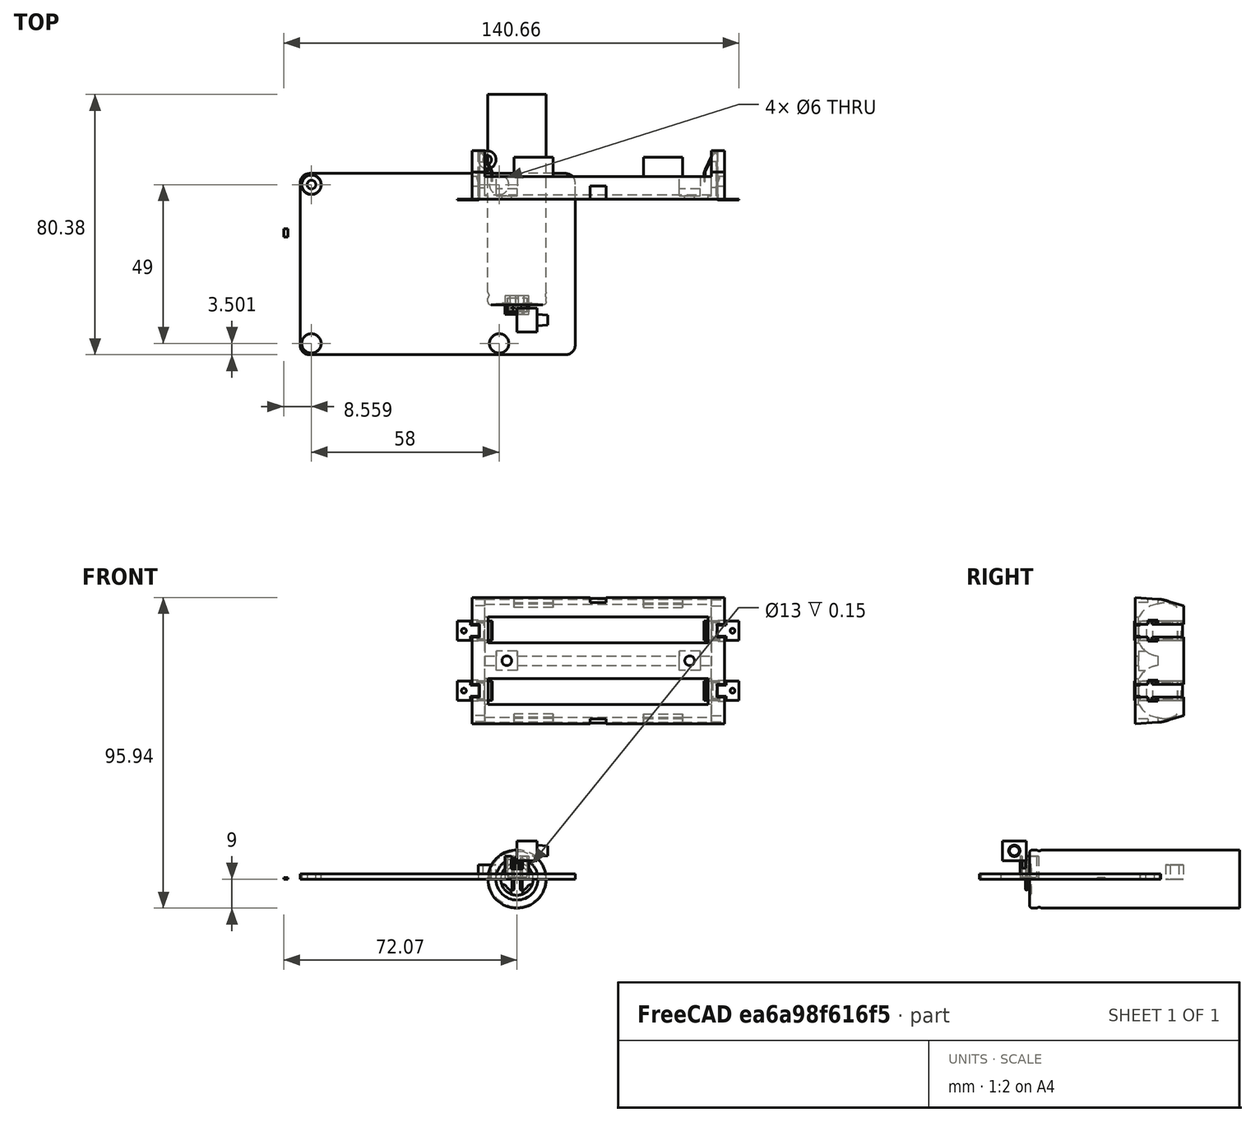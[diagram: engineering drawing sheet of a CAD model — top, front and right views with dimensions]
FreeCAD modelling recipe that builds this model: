
FCSTD DOCUMENT  (FreeCAD 1.0R39109 (Git))
Label: UPS
License: All rights reserved
LicenseURL: https://en.wikipedia.org/wiki/All_rights_reserved
objects: App::FeaturePython×23, App::Link×22, Part::Feature×12, Sketcher::SketchObject×6, PartDesign::Pad×6, PartDesign::Body×5, App::Part×4, PartDesign::Chamfer×1, Assembly::JointGroup×1, Assembly::AssemblyObject×1
note: 50 computed .brp shape members not serialized (recipe doc carries the construction recipe); baked Part::Feature solids carry a one-line shape summary decoded from their .brp

FEATURE [Sketcher::SketchObject] Sketch
  ArcFitTolerance = 1e-06
  FullyConstrained = false
  MakeInternals = false
  sketch-geometry (20):
    g0: LineSegment StartX=-64.0111 StartY=-15.3795 StartZ=0 EndX=14.9889 EndY=-15.3795 EndZ=0
    g1: LineSegment StartX=17.9889 StartY=-12.3795 StartZ=0 EndX=17.9889 EndY=37.6205 EndZ=0
    g2: LineSegment StartX=14.9889 StartY=40.6205 StartZ=0 EndX=-64.0111 EndY=40.6205 EndZ=0
    g3: LineSegment StartX=-67.0111 StartY=37.6205 StartZ=0 EndX=-67.0111 EndY=-12.3795 EndZ=0
    g4: ArcOfCircle CenterX=14.9889 CenterY=37.6205 CenterZ=0 NormalX=0 NormalY=0 NormalZ=1 AngleXU=0 Radius=3 StartAngle=5e-16 EndAngle=1.5708
    g5: GeomPoint [constr] X=17.9889 Y=40.6205 Z=0
    g6: ArcOfCircle CenterX=-64.0111 CenterY=37.6205 CenterZ=0 NormalX=0 NormalY=0 NormalZ=1 AngleXU=0 Radius=3 StartAngle=1.5708 EndAngle=3.14159
    g7: GeomPoint [constr] X=-67.0111 Y=40.6205 Z=0
    g8: ArcOfCircle CenterX=-64.0111 CenterY=-12.3795 CenterZ=0 NormalX=0 NormalY=0 NormalZ=1 AngleXU=0 Radius=3 StartAngle=3.14159 EndAngle=4.71239
    g9: GeomPoint [constr] X=-67.0111 Y=-15.3795 Z=0
    g10: ArcOfCircle CenterX=14.9889 CenterY=-12.3795 CenterZ=0 NormalX=0 NormalY=0 NormalZ=1 AngleXU=0 Radius=3 StartAngle=4.71239 EndAngle=6.28319
    g11: GeomPoint [constr] X=17.9889 Y=-15.3795 Z=0
    g12: Circle CenterX=-63.5111 CenterY=37.1205 CenterZ=0 NormalX=0 NormalY=0 NormalZ=1 AngleXU=0 Radius=1.35
    g13: Circle CenterX=-63.5111 CenterY=37.1205 CenterZ=0 NormalX=0 NormalY=0 NormalZ=1 AngleXU=0 Radius=3
    g14: Circle CenterX=-63.5111 CenterY=-11.8795 CenterZ=0 NormalX=0 NormalY=0 NormalZ=1 AngleXU=0 Radius=1.35
    g15: Circle CenterX=-63.5111 CenterY=-11.8795 CenterZ=0 NormalX=0 NormalY=0 NormalZ=1 AngleXU=0 Radius=3
    g16: Circle CenterX=-5.51111 CenterY=37.1205 CenterZ=0 NormalX=0 NormalY=0 NormalZ=1 AngleXU=0 Radius=1.35
    g17: Circle CenterX=-5.51111 CenterY=37.1205 CenterZ=0 NormalX=0 NormalY=0 NormalZ=1 AngleXU=0 Radius=3
    g18: Circle CenterX=-5.51111 CenterY=-11.8795 CenterZ=0 NormalX=0 NormalY=0 NormalZ=1 AngleXU=0 Radius=1.35
    g19: Circle CenterX=-5.51111 CenterY=-11.8795 CenterZ=0 NormalX=0 NormalY=0 NormalZ=1 AngleXU=0 Radius=3
  constraints (46):
    c: Horizontal(g0)
    c: Horizontal(g2)
    c: Vertical(g1)
    c: Vertical(g3)
    c: DistanceX(g7,g5) = 85
    c: DistanceY(g9,g7) = 56
    c: PointOnObject(g5,g1)
    c: PointOnObject(g5,g2)
    c: Tangent(g1,g4) = -1.5708
    c: Tangent(g2,g4) = -1.5708
    c: PointOnObject(g7,g2)
    c: PointOnObject(g7,g3)
    c: Tangent(g2,g6) = -1.5708
    c: Tangent(g3,g6) = -1.5708
    c: PointOnObject(g9,g0)
    c: PointOnObject(g9,g3)
    c: Tangent(g0,g8) = -1.5708
    c: Tangent(g3,g8) = -1.5708
    c: PointOnObject(g11,g0)
    c: PointOnObject(g11,g1)
    c: Tangent(g0,g10) = -1.5708
    c: Tangent(g1,g10) = -1.5708
    c: Radius(g6) = 3
    c: Radius(g8) = 3
    c: Radius(g4) = 3
    c: Radius(g10) = 3
    c: Diameter(g12) = 2.7
    c: Coincident(g13,g12)
    c: Diameter(g13) = 6
    c: Diameter(g14) = 2.7
    c: Coincident(g15,g14)
    c: Diameter(g15) = 6
    c: Vertical(g14,g12)
    c: Distance(g13,g15) = 43
    c: Distance(g13,g3) = 0.5
    c: Distance(g13,g2) = 0.5
    c: Diameter(g16) = 2.7
    c: Coincident(g17,g16)
    c: Diameter(g17) = 6
    c: Diameter(g18) = 2.7
    c: Coincident(g19,g18)
    c: Diameter(g19) = 6
    c: Vertical(g18,g16)
    c: Distance(g17,g19) = 43
    c: Distance(g15,g19) = 52
    c: Horizontal(g18,g14)
FEATURE [PartDesign::Pad] Pad
  Direction = (0,0,1)
  Length = 1.6
  Length2 = 10
  Profile = -> Sketch
  ReferenceAxis = -> Sketch [N_Axis]
  Refine = true
  Suppressed = false
  Type = 0
FEATURE [PartDesign::Body] Body  label="Board"
  AllowCompound = false
  Group = -> [Sketch,Pad]
  Origin = -> Origin
  Tip = -> Pad
FEATURE [Sketcher::SketchObject] Sketch001
  ArcFitTolerance = 1e-06
  AttachmentSupport = -> [XY_Plane003]
  FullyConstrained = false
  MakeInternals = false
  MapMode = 5
  sketch-geometry (2):
    g0: Circle CenterX=-63.4811 CenterY=37.1626 CenterZ=0 NormalX=0 NormalY=0 NormalZ=1 AngleXU=0 Radius=3
    g1: Circle CenterX=-63.4811 CenterY=37.1626 CenterZ=0 NormalX=0 NormalY=0 NormalZ=1 AngleXU=0 Radius=1.35
  constraints (3):
    c: Diameter(g0) = 6
    c: Coincident(g1,g0)
    c: Diameter(g1) = 2.7
FEATURE [PartDesign::Pad] Pad001
  Direction = (0,0,1)
  Length = 1.6
  Length2 = 10
  Profile = -> Sketch001
  ReferenceAxis = -> Sketch001 [N_Axis]
  Refine = true
  Suppressed = false
  Type = 0
FEATURE [PartDesign::Body] Body001  label="Screw Insert"
  AllowCompound = false
  Group = -> [Sketch001,Pad001]
  Origin = -> Origin003
  Tip = -> Pad001
FEATURE [Part::Feature] Part__Feature  label="Battery Holder"
  Placement = pos=(25.0935,32.6929,67.437) rot=(0,0,1;0rad)
  shape: bbox 78 x 15 x 39 mm, 194 faces (baked)
FEATURE [Part::Feature] Part__Feature001  label="Battery-Holder_Metal-Lead"
  Placement = pos=(66.5935,32.3929,76.687) rot=(0,0,1;0rad)
  shape: bbox 10.8 x 15.51 x 6 mm, 51 faces (baked)
FEATURE [Part::Feature] Part__Feature002  label="Battery-Holder_Metal-Lead001"
  Placement = pos=(66.5935,32.3929,58.187) rot=(0,0,1;0rad)
  shape: bbox 10.8 x 15.51 x 6 mm, 51 faces (baked)
FEATURE [Part::Feature] Part__Feature003  label="Battery-Holder_Metal-Lead002"
  Placement = pos=(-16.4065,32.3929,58.187) rot=(0,1,0;3.14159rad)
  shape: bbox 10.8 x 15.51 x 6 mm, 51 faces (baked)
FEATURE [Part::Feature] Part__Feature004  label="Battery-Holder_Metal-Lead003"
  Placement = pos=(-16.4065,32.3929,76.687) rot=(0,1,0;3.14159rad)
  shape: bbox 10.8 x 15.51 x 6 mm, 51 faces (baked)
FEATURE [App::Part] Assem1  label="18650 Battery Holder"
  Group = -> [Part__Feature,Part__Feature001,Part__Feature002,Part__Feature003,Part__Feature004]
  Origin = -> Origin004
FEATURE [Part::Feature] Part__Feature005  label="18650 v1"
  shape: bbox 19.48 x 65 x 19.48 mm, 40 faces (baked)
FEATURE [App::FeaturePython] Temporary_joint  # Assembly joint (typed FeaturePython)
  Activated = true
  AngleMax = 0
  AngleMin = 0
  Detach1 = false
  Detach2 = false
  Distance = 0
  Distance2 = 0
  EnableAngleMax = false
  EnableAngleMin = false
  EnableLengthMax = false
  EnableLengthMin = false
  JointType = 0 (Fixed)
  LengthMax = 0
  LengthMin = 0
FEATURE [App::Link] Board  label="Board001"
  LinkedObject = -> Body
FEATURE [App::FeaturePython] GroundedJoint  # Assembly grounded joint (typed FeaturePython)
  ObjectToGround = -> Board
FEATURE [App::Link] _8650_Battery_Holder  label="18650 Battery Holder001"
  LinkPlacement = pos=(-46.1046,82.0575,-31.0929) rot=(1,0,0;1.5708rad)
  LinkedObject = -> Assem1
  Placement = pos=(-46.1046,82.0575,-31.0929) rot=(1,0,0;1.5708rad)
FEATURE [App::Link] Screw_Insert  label="Screw Insert001"
  LinkPlacement = pos=(-0.030029,-0.0421514,0) rot=(0,0,1;0rad)
  LinkedObject = -> Body001
  Placement = pos=(-0.030029,-0.0421514,0) rot=(0,0,1;0rad)
FEATURE [App::Link] Screw_Insert001  label="Screw Insert002"
  LinkPlacement = pos=(-0.030029,-49.0422,1e-16) rot=(0,0,1;0rad)
  LinkedObject = -> Body001
  Placement = pos=(-0.030029,-49.0422,1e-16) rot=(0,0,1;0rad)
FEATURE [App::Link] Screw_Insert002  label="Screw Insert003"
  LinkPlacement = pos=(57.97,-49.0422,-1e-16) rot=(0,0,1;0rad)
  LinkedObject = -> Body001
  Placement = pos=(57.97,-49.0422,-1e-16) rot=(0,0,1;0rad)
FEATURE [App::Link] Screw_Insert003  label="Screw Insert004"
  LinkPlacement = pos=(57.97,-0.0421514,0) rot=(0,0,1;0rad)
  LinkedObject = -> Body001
  Placement = pos=(57.97,-0.0421514,0) rot=(0,0,1;0rad)
FEATURE [App::FeaturePython] Joint  label="Fixed"  # Assembly joint (typed FeaturePython)
  Activated = true
  AngleMax = 0
  AngleMin = 0
  Detach1 = false
  Detach2 = false
  Distance = 0
  Distance2 = 0
  EnableAngleMax = false
  EnableAngleMin = false
  EnableLengthMax = false
  EnableLengthMin = false
  JointType = 0 (Fixed)
  LengthMax = 0
  LengthMin = 0
  Placement1 = pos=(-63.4811,37.1626,1.6) rot=(0,0,1;0rad)
  Placement2 = pos=(-63.5111,37.1205,1.6) rot=(0,0,1;0rad)
  Reference1 = -> Assembly [Screw_Insert.Edge3,Screw_Insert.Edge3]
  Reference2 = -> Assembly [Board.Edge36,Board.Edge36]
FEATURE [App::FeaturePython] Joint001  label="Fixed001"  # Assembly joint (typed FeaturePython)
  Activated = true
  AngleMax = 0
  AngleMin = 0
  Detach1 = false
  Detach2 = false
  Distance = 0
  Distance2 = 0
  EnableAngleMax = false
  EnableAngleMin = false
  EnableLengthMax = false
  EnableLengthMin = false
  JointType = 0 (Fixed)
  LengthMax = 0
  LengthMin = 0
  Placement1 = pos=(-63.4811,37.1626,1.6) rot=(0,0,1;0rad)
  Placement2 = pos=(-63.5111,-11.8795,1.6) rot=(0,0,1;0rad)
  Reference1 = -> Assembly [Screw_Insert001.Edge3,Screw_Insert001.Edge3]
  Reference2 = -> Assembly [Board.Edge33,Board.Edge33]
FEATURE [App::FeaturePython] Joint002  label="Fixed002"  # Assembly joint (typed FeaturePython)
  Activated = true
  AngleMax = 0
  AngleMin = 0
  Detach1 = false
  Detach2 = false
  Distance = 0
  Distance2 = 0
  EnableAngleMax = false
  EnableAngleMin = false
  EnableLengthMax = false
  EnableLengthMin = false
  JointType = 0 (Fixed)
  LengthMax = 0
  LengthMin = 0
  Placement1 = pos=(-63.4811,37.1626,1.6) rot=(0,0,1;0rad)
  Placement2 = pos=(-5.51111,-11.8795,1.6) rot=(0,0,1;0rad)
  Reference1 = -> Assembly [Screw_Insert002.Edge3,Screw_Insert002.Edge3]
  Reference2 = -> Assembly [Board.Edge27,Board.Edge27]
FEATURE [App::FeaturePython] Joint003  label="Fixed003"  # Assembly joint (typed FeaturePython)
  Activated = true
  AngleMax = 0
  AngleMin = 0
  Detach1 = false
  Detach2 = false
  Distance = 0
  Distance2 = 0
  EnableAngleMax = false
  EnableAngleMin = false
  EnableLengthMax = false
  EnableLengthMin = false
  JointType = 0 (Fixed)
  LengthMax = 0
  LengthMin = 0
  Placement1 = pos=(-63.4811,37.1626,1.6) rot=(0,0,1;0rad)
  Placement2 = pos=(-5.51111,37.1205,1.6) rot=(0,0,1;0rad)
  Reference1 = -> Assembly [Screw_Insert003.Edge3,Screw_Insert003.Edge3]
  Reference2 = -> Assembly [Board.Edge30,Board.Edge30]
FEATURE [Part::Feature] Part__Feature006  label="XH 2,54_2p"
  shape: bbox 7.4 x 5.75 x 7 mm, 52 faces (baked)
FEATURE [Part::Feature] Part__Feature007  label="XH 2,54_2p001"
  shape: bbox 0.64 x 0.64 x 9.7 mm, 14 faces (baked)
FEATURE [Part::Feature] Part__Feature008  label="XH 2,54_2p002"
  shape: bbox 0.64 x 0.64 x 9.7 mm, 14 faces (baked)
FEATURE [App::Part] XH_2_54_2p  label="XH 2,54_2p003"
  Group = -> [Part__Feature006,Part__Feature007,Part__Feature008]
  Origin = -> Origin006
FEATURE [Part::Feature] Part__Feature009  label="XH 2,54_2p004"
  shape: bbox 7.4 x 5.75 x 7 mm, 52 faces (baked)
FEATURE [Part::Feature] Part__Feature010  label="XH 2,54_2p005"
  shape: bbox 0.64 x 0.64 x 9.7 mm, 14 faces (baked)
FEATURE [Part::Feature] Part__Feature011  label="XH 2,54_2p006"
  shape: bbox 0.64 x 0.64 x 9.7 mm, 14 faces (baked)
FEATURE [App::Part] XH_2_54_2p001  label="XH 2,54_2p007"
  Group = -> [Part__Feature009,Part__Feature010,Part__Feature011]
  Origin = -> Origin007
FEATURE [App::Link] XH_2_54_2p007  label="XH 2,54_2p008"
  LinkPlacement = pos=(-33.6111,-12.3795,1.6) rot=(0,0,1;0rad)
  LinkedObject = -> XH_2_54_2p001
  Placement = pos=(-33.6111,-12.3795,1.6) rot=(0,0,1;0rad)
FEATURE [App::Link] XH_2_54_2p008  label="XH 2,54_2p009"
  LinkPlacement = pos=(5.78889,-12.3795,1.6) rot=(0,0,1;0rad)
  LinkedObject = -> XH_2_54_2p001
  Placement = pos=(5.78889,-12.3795,1.6) rot=(0,0,1;0rad)
FEATURE [App::FeaturePython] Joint004  label="Fixed004"  # Assembly joint (typed FeaturePython)
  Activated = true
  AngleMax = 0
  AngleMin = 0
  Detach1 = false
  Detach2 = false
  Distance = 0
  Distance2 = 0
  EnableAngleMax = false
  EnableAngleMin = false
  EnableLengthMax = false
  EnableLengthMin = false
  JointType = 0 (Fixed)
  LengthMax = 0
  LengthMin = 0
  Offset1 = pos=(0,8.5,0) rot=(0,0,1;0rad)
  Placement1 = pos=(12.2,0,0) rot=(0.57735,0.57735,0.57735;4.18879rad)
  Placement2 = pos=(17.9889,-12.3795,1.6) rot=(0.57735,0.57735,0.57735;4.18879rad)
  Reference1 = -> Assembly [XH_2_54_2p008.Part__Feature009.Edge98,XH_2_54_2p008.Part__Feature009.Edge98]
  Reference2 = -> Assembly [Board.Edge10,Board.Vertex6]
FEATURE [App::FeaturePython] Joint005  label="Fixed005"  # Assembly joint (typed FeaturePython)
  Activated = true
  AngleMax = 0
  AngleMin = 0
  Detach1 = false
  Detach2 = false
  Distance = 0
  Distance2 = 0
  EnableAngleMax = false
  EnableAngleMin = false
  EnableLengthMax = false
  EnableLengthMin = false
  JointType = 0 (Fixed)
  LengthMax = 0
  LengthMin = 0
  Offset1 = pos=(0,32,0) rot=(0,0,1;0rad)
  Offset2 = pos=(0,0,0) rot=(0,0,1;3.14159rad)
  Placement1 = pos=(35.7,0,0) rot=(0.57735,0.57735,0.57735;4.18879rad)
  Placement2 = pos=(-3.7,0,0) rot=(-0.57735,0.57735,-0.57735;4.18879rad)
  Reference1 = -> Assembly [XH_2_54_2p007.Part__Feature009.Edge98,XH_2_54_2p007.Part__Feature009.Edge98]
  Reference2 = -> Assembly [XH_2_54_2p008.Part__Feature009.Edge75,XH_2_54_2p008.Part__Feature009.Edge75]
FEATURE [App::FeaturePython] Joint006  label="Fixed006"  # Assembly joint (typed FeaturePython)
  Activated = true
  AngleMax = 0
  AngleMin = 0
  Detach1 = false
  Detach2 = false
  Distance = 0
  Distance2 = 0
  EnableAngleMax = false
  EnableAngleMin = false
  EnableLengthMax = false
  EnableLengthMin = false
  JointType = 0 (Fixed)
  LengthMax = 0
  LengthMin = 0
  Offset2 = pos=(0,0,2) rot=(0,0,-1;1.5708rad)
  Placement1 = pos=(39,7.1e-15,0) rot=(0,1,0;3.14159rad)
  Placement2 = pos=(17.9889,14.6205,1.6) rot=(0,0.707107,0.707107;3.14159rad)
  Reference1 = -> Assembly [_8650_Battery_Holder.Part__Feature.Edge41,_8650_Battery_Holder.Part__Feature.Edge41]
  Reference2 = -> Assembly [Board.Edge10,Board.Edge10]
FEATURE [App::Link] _8650_v1  label="18650 v002"
  LinkPlacement = pos=(11.2889,5.37045,11.2138) rot=(0,0,1;1.5708rad)
  LinkedObject = -> Part__Feature005
  Placement = pos=(11.2889,5.37045,11.2138) rot=(0,0,1;1.5708rad)
FEATURE [App::Link] _8650_v002  label="18650 v003"
  LinkPlacement = pos=(11.2889,23.8705,11.2138) rot=(0,0,1;1.5708rad)
  LinkedObject = -> Part__Feature005
  Placement = pos=(11.2889,23.8705,11.2138) rot=(0,0,1;1.5708rad)
FEATURE [App::FeaturePython] Joint007  label="Fixed007"  # Assembly joint (typed FeaturePython)
  Activated = true
  AngleMax = 0
  AngleMin = 0
  Detach1 = false
  Detach2 = false
  Distance = 0
  Distance2 = 0
  EnableAngleMax = false
  EnableAngleMin = false
  EnableLengthMax = false
  EnableLengthMin = false
  JointType = 0 (Fixed)
  LengthMax = 0
  LengthMin = 0
  Offset1 = pos=(-3,0,0) rot=(0,0,1;0rad)
  Placement1 = pos=(-5e-16,65,-3) rot=(-0.57735,-0.57735,-0.57735;2.0944rad)
  Placement2 = pos=(-8.8,6.91375,0) rot=(-0.57735,-0.57735,-0.57735;4.18879rad)
  Reference1 = -> Assembly [_8650_v1.Face35,_8650_v1.Edge1]
  Reference2 = -> Assembly [_8650_Battery_Holder.Part__Feature004.Face22,_8650_Battery_Holder.Part__Feature004.Face22]
FEATURE [App::FeaturePython] Joint008  label="Fixed008"  # Assembly joint (typed FeaturePython)
  Activated = true
  AngleMax = 0
  AngleMin = 0
  Detach1 = false
  Detach2 = false
  Distance = 0
  Distance2 = 0
  EnableAngleMax = false
  EnableAngleMin = false
  EnableLengthMax = false
  EnableLengthMin = false
  JointType = 0 (Fixed)
  LengthMax = 0
  LengthMin = 0
  Offset1 = pos=(-3,0,0) rot=(0,0,1;0rad)
  Placement1 = pos=(-5e-16,65,-3) rot=(-0.57735,-0.57735,-0.57735;2.0944rad)
  Placement2 = pos=(-8.8,6.91375,0) rot=(-0.57735,-0.57735,-0.57735;4.18879rad)
  Reference1 = -> Assembly [_8650_v002.Face35,_8650_v002.Face35]
  Reference2 = -> Assembly [_8650_Battery_Holder.Part__Feature003.Face22,_8650_Battery_Holder.Part__Feature003.Face22]
FEATURE [Sketcher::SketchObject] Sketch002
  ArcFitTolerance = 1e-06
  AttachmentSupport = -> [XY_Plane008]
  FullyConstrained = false
  MakeInternals = false
  MapMode = 5
  sketch-geometry (2):
    g0: Circle CenterX=-9.21613 CenterY=44.8635 CenterZ=0 NormalX=0 NormalY=0 NormalZ=1 AngleXU=0 Radius=2.75
    g1: Circle CenterX=-9.21613 CenterY=44.8635 CenterZ=0 NormalX=0 NormalY=0 NormalZ=1 AngleXU=0 Radius=1.35
  constraints (3):
    c: Diameter(g0) = 5.5
    c: Coincident(g1,g0)
    c: Diameter(g1) = 2.7
FEATURE [PartDesign::Pad] Pad002
  Direction = (0,0,1)
  Length = 4.4
  Length2 = 10
  Profile = -> Sketch002
  ReferenceAxis = -> Sketch002 [N_Axis]
  Refine = true
  Suppressed = false
  Type = 0
FEATURE [PartDesign::Body] Body002  label="Spacer"
  AllowCompound = false
  Group = -> [Sketch002,Pad002]
  Origin = -> Origin008
  Tip = -> Pad002
FEATURE [Sketcher::SketchObject] Sketch003
  ArcFitTolerance = 1e-06
  AttachmentSupport = -> [YZ_Plane009]
  FullyConstrained = false
  MakeInternals = false
  MapMode = 5
  Placement = pos=(0,0,0) rot=(0.57735,0.57735,0.57735;2.0944rad)
  sketch-geometry (4):
    g0: LineSegment StartX=-8.34718 StartY=11.7111 StartZ=0 EndX=-8.34718 EndY=5.71105 EndZ=0
    g1: LineSegment StartX=-8.34718 StartY=5.71105 StartZ=0 EndX=-0.947178 EndY=5.71105 EndZ=0
    g2: LineSegment StartX=-0.947178 StartY=5.71105 StartZ=0 EndX=-0.947178 EndY=11.7111 EndZ=0
    g3: LineSegment StartX=-0.947178 StartY=11.7111 StartZ=0 EndX=-8.34718 EndY=11.7111 EndZ=0
  constraints (10):
    c: Coincident(g0,g1)
    c: Coincident(g1,g2)
    c: Coincident(g2,g3)
    c: Coincident(g3,g0)
    c: Vertical(g0)
    c: Vertical(g2)
    c: Horizontal(g1)
    c: Horizontal(g3)
    c: DistanceX(g3,g3) = 7.4
    c: DistanceY(g0,g0) = 6
FEATURE [PartDesign::Pad] Pad003
  Direction = (1,0,0)
  Length = 6.25
  Length2 = 10
  Placement = pos=(0,0,0) rot=(1,1,1;2.0944rad)
  Profile = -> Sketch003
  ReferenceAxis = -> Sketch003 [N_Axis]
  Refine = true
  Suppressed = false
  Type = 0
FEATURE [Sketcher::SketchObject] Sketch004
  ArcFitTolerance = 1e-06
  AttachmentSupport = -> [Pad003]
  ExternalGeometry = -> [Pad003]
  FullyConstrained = true
  MakeInternals = false
  MapMode = 5
  Placement = pos=(6.25,-1.4e-15,7e-16) rot=(0.57735,0.57735,0.57735;2.0944rad)
  sketch-geometry (3):
    g0: GeomPoint X=-4.64718 Y=11.7111 Z=0
    g1: GeomPoint X=-8.34718 Y=8.71105 Z=0
    g2: Circle CenterX=-4.64718 CenterY=8.71105 CenterZ=0 NormalX=0 NormalY=0 NormalZ=1 AngleXU=0 Radius=1.5
  constraints (5):
    c: Symmetric(g-3,g-3,g0)
    c: Symmetric(g-4,g-4,g1)
    c: Diameter(g2) = 3
    c: Vertical(g2,g0)
    c: Horizontal(g1,g2)
FEATURE [PartDesign::Pad] Pad004
  BaseFeature = -> Pad003
  Direction = (1,0,0)
  Length = 3.25
  Length2 = 10
  Placement = pos=(0,0,0) rot=(1,1,1;2.0944rad)
  Profile = -> Sketch004
  ReferenceAxis = -> Sketch004 [N_Axis]
  Refine = true
  Suppressed = false
  Type = 0
FEATURE [PartDesign::Chamfer] Chamfer
  Angle = 85.55
  Base = -> Pad004 [Edge13]
  BaseFeature = -> Pad004
  ChamferType = 2
  FlipDirection = false
  Placement = pos=(0,0,0) rot=(1,1,1;2.0944rad)
  Refine = true
  Size = 0.25
  Size2 = 1
  SupportTransform = false
  Suppressed = false
  UseAllEdges = false
FEATURE [PartDesign::Body] Body003  label="Button"
  AllowCompound = false
  Group = -> [Sketch003,Pad003,Sketch004,Pad004,Chamfer]
  Origin = -> Origin009
  Tip = -> Chamfer
FEATURE [App::Link] Button  label="Button001"
  LinkPlacement = pos=(-60.7611,-6.52673,-3.31105) rot=(0,0,1;3.14159rad)
  LinkedObject = -> Body003
  Placement = pos=(-60.7611,-6.52673,-3.31105) rot=(0,0,1;3.14159rad)
FEATURE [App::Link] Spacer  label="Spacer001"
  LinkPlacement = pos=(-54.295,-56.7431,-4.4) rot=(0,0,1;0rad)
  LinkedObject = -> Body002
  Placement = pos=(-54.295,-56.7431,-4.4) rot=(0,0,1;0rad)
FEATURE [App::Link] Spacer001  label="Spacer002"
  LinkPlacement = pos=(3.70503,-56.7431,-4.4) rot=(0,0,1;0rad)
  LinkedObject = -> Body002
  Placement = pos=(3.70503,-56.7431,-4.4) rot=(0,0,1;0rad)
FEATURE [App::Link] Spacer002  label="Spacer003"
  LinkPlacement = pos=(-54.295,-7.74309,-4.4) rot=(0,0,1;0rad)
  LinkedObject = -> Body002
  Placement = pos=(-54.295,-7.74309,-4.4) rot=(0,0,1;0rad)
FEATURE [App::Link] Spacer003  label="Spacer004"
  LinkPlacement = pos=(3.70503,-7.74309,-4.4) rot=(0,0,1;0rad)
  LinkedObject = -> Body002
  Placement = pos=(3.70503,-7.74309,-4.4) rot=(0,0,1;0rad)
FEATURE [App::FeaturePython] Joint009  label="Fixed009"  # Assembly joint (typed FeaturePython)
  Activated = true
  AngleMax = 0
  AngleMin = 0
  Detach1 = false
  Detach2 = false
  Distance = 0
  Distance2 = 0
  EnableAngleMax = false
  EnableAngleMin = false
  EnableLengthMax = false
  EnableLengthMin = false
  JointType = 0 (Fixed)
  LengthMax = 0
  LengthMin = 0
  Offset2 = pos=(-0.8,0,-10.5) rot=(0,0,1;3.14159rad)
  Placement1 = pos=(6.25,-4.64718,5.71105) rot=(0.57735,0.57735,0.57735;4.18879rad)
  Placement2 = pos=(-67.0111,-1.87955,2.4) rot=(-0.57735,0.57735,-0.57735;4.18879rad)
  Reference1 = -> Assembly [Button.Edge4,Button.Edge4]
  Reference2 = -> Assembly [Board.Edge22,Board.Vertex16]
FEATURE [App::FeaturePython] Joint010  label="Fixed010"  # Assembly joint (typed FeaturePython)
  Activated = true
  AngleMax = 0
  AngleMin = 0
  Detach1 = false
  Detach2 = false
  Distance = 0
  Distance2 = 0
  EnableAngleMax = false
  EnableAngleMin = false
  EnableLengthMax = false
  EnableLengthMin = false
  JointType = 0 (Fixed)
  LengthMax = 0
  LengthMin = 0
  Placement1 = pos=(-9.21613,44.8635,4.4) rot=(0,0,1;0rad)
  Placement2 = pos=(-5.51111,37.1205,0) rot=(0,0,1;0rad)
  Reference1 = -> Assembly [Spacer003.Edge3,Spacer003.Edge3]
  Reference2 = -> Assembly [Board.Edge29,Board.Edge29]
FEATURE [App::FeaturePython] Joint011  label="Fixed011"  # Assembly joint (typed FeaturePython)
  Activated = true
  AngleMax = 0
  AngleMin = 0
  Detach1 = false
  Detach2 = false
  Distance = 0
  Distance2 = 0
  EnableAngleMax = false
  EnableAngleMin = false
  EnableLengthMax = false
  EnableLengthMin = false
  JointType = 0 (Fixed)
  LengthMax = 0
  LengthMin = 0
  Placement1 = pos=(-9.21613,44.8635,4.4) rot=(0,0,1;0rad)
  Placement2 = pos=(-63.5111,37.1205,0) rot=(0,0,1;0rad)
  Reference1 = -> Assembly [Spacer002.Edge3,Spacer002.Edge3]
  Reference2 = -> Assembly [Board.Edge35,Board.Edge35]
FEATURE [App::FeaturePython] Joint012  label="Fixed012"  # Assembly joint (typed FeaturePython)
  Activated = true
  AngleMax = 0
  AngleMin = 0
  Detach1 = false
  Detach2 = false
  Distance = 0
  Distance2 = 0
  EnableAngleMax = false
  EnableAngleMin = false
  EnableLengthMax = false
  EnableLengthMin = false
  JointType = 0 (Fixed)
  LengthMax = 0
  LengthMin = 0
  Placement1 = pos=(-9.21613,44.8635,4.4) rot=(0,0,1;0rad)
  Placement2 = pos=(-63.4811,37.1626,0) rot=(0,0,1;0rad)
  Reference1 = -> Assembly [Spacer.Edge3,Spacer.Edge3]
  Reference2 = -> Assembly [Screw_Insert001.Edge2,Screw_Insert001.Edge2]
FEATURE [App::FeaturePython] Joint013  label="Fixed013"  # Assembly joint (typed FeaturePython)
  Activated = true
  AngleMax = 0
  AngleMin = 0
  Detach1 = false
  Detach2 = false
  Distance = 0
  Distance2 = 0
  EnableAngleMax = false
  EnableAngleMin = false
  EnableLengthMax = false
  EnableLengthMin = false
  JointType = 0 (Fixed)
  LengthMax = 0
  LengthMin = 0
  Placement1 = pos=(-9.21613,44.8635,4.4) rot=(0,0,1;0rad)
  Placement2 = pos=(-63.4811,37.1626,0) rot=(0,0,1;0rad)
  Reference1 = -> Assembly [Spacer001.Edge3,Spacer001.Edge3]
  Reference2 = -> Assembly [Screw_Insert002.Edge2,Screw_Insert002.Edge2]
FEATURE [Sketcher::SketchObject] Sketch005
  ArcFitTolerance = 1e-06
  AttachmentSupport = -> [XY_Plane010]
  FullyConstrained = false
  MakeInternals = false
  MapMode = 5
  sketch-geometry (4):
    g0: LineSegment StartX=-72.0667 StartY=23.4887 StartZ=0 EndX=-72.0667 EndY=20.9887 EndZ=0
    g1: LineSegment StartX=-72.0667 StartY=20.9887 StartZ=0 EndX=-70.8167 EndY=20.9887 EndZ=0
    g2: LineSegment StartX=-70.8167 StartY=20.9887 StartZ=0 EndX=-70.8167 EndY=23.4887 EndZ=0
    g3: LineSegment StartX=-70.8167 StartY=23.4887 StartZ=0 EndX=-72.0667 EndY=23.4887 EndZ=0
  constraints (10):
    c: Coincident(g0,g1)
    c: Coincident(g1,g2)
    c: Coincident(g2,g3)
    c: Coincident(g3,g0)
    c: Vertical(g0)
    c: Vertical(g2)
    c: Horizontal(g1)
    c: Horizontal(g3)
    c: DistanceY(g2,g2) = 2.5
    c: Distance(g3,g3) = 1.25
FEATURE [PartDesign::Pad] Pad005
  Direction = (0,0,1)
  Length = 0.5
  Length2 = 10
  Profile = -> Sketch005
  ReferenceAxis = -> Sketch005 [N_Axis]
  Refine = true
  Suppressed = false
  Type = 0
FEATURE [PartDesign::Body] Body004  label="LED"
  AllowCompound = false
  Group = -> [Sketch005,Pad005]
  Origin = -> Origin010
  Tip = -> Pad005
FEATURE [App::Part] Part  label="Parts001"
  Group = -> [Body,Body001,Temporary_joint,Body002,Body003,Body004]
  Origin = -> Origin002
FEATURE [App::Link] LED  label="LED001"
  LinkPlacement = pos=(6.15556,-2.86826,-0.5) rot=(0,0,1;0rad)
  LinkedObject = -> Body004
  Placement = pos=(6.15556,-2.86826,-0.5) rot=(0,0,1;0rad)
FEATURE [App::Link] LED001  label="LED002"
  LinkPlacement = pos=(-136.728,-16.3683,0) rot=(0,1,0;3.14159rad)
  LinkedObject = -> Body004
  Placement = pos=(-136.728,-16.3683,0) rot=(0,1,0;3.14159rad)
FEATURE [App::Link] LED002  label="LED003"
  LinkPlacement = pos=(-136.728,7.13174,4.4e-15) rot=(0,1,0;3.14159rad)
  LinkedObject = -> Body004
  Placement = pos=(-136.728,7.13174,4.4e-15) rot=(0,1,0;3.14159rad)
FEATURE [App::Link] LED003  label="LED004"
  LinkPlacement = pos=(-136.728,-7.36826,0) rot=(0,1,0;3.14159rad)
  LinkedObject = -> Body004
  Placement = pos=(-136.728,-7.36826,0) rot=(0,1,0;3.14159rad)
FEATURE [App::Link] LED004  label="LED005"
  LinkPlacement = pos=(6.15556,-11.8683,-0.5) rot=(0,0,1;0rad)
  LinkedObject = -> Body004
  Placement = pos=(6.15556,-11.8683,-0.5) rot=(0,0,1;0rad)
FEATURE [App::Link] LED005  label="LED006"
  LinkPlacement = pos=(-25.0224,56.8621,-0.5) rot=(0,0,1;1.5708rad)
  LinkedObject = -> Body004
  Placement = pos=(-25.0224,56.8621,-0.5) rot=(0,0,1;1.5708rad)
FEATURE [App::Link] LED006  label="LED007"
  LinkPlacement = pos=(-20.0224,-86.0212,-1.79e-14) rot=(-0.707107,0.707107,0;3.14159rad)
  LinkedObject = -> Body004
  Placement = pos=(-20.0224,-86.0212,-1.79e-14) rot=(-0.707107,0.707107,0;3.14159rad)
FEATURE [App::FeaturePython] Joint014  label="Fixed014"  # Assembly joint (typed FeaturePython)
  Activated = true
  AngleMax = 0
  AngleMin = 0
  Detach1 = false
  Detach2 = false
  Distance = 0
  Distance2 = 0
  EnableAngleMax = false
  EnableAngleMin = false
  EnableLengthMax = false
  EnableLengthMin = false
  JointType = 0 (Fixed)
  LengthMax = 0
  LengthMin = 0
  Offset2 = pos=(0,0,-2) rot=(0,0,1;0rad)
  Placement1 = pos=(-71.4417,23.4887,0.25) rot=(0,-0.707107,0.707107;3.14159rad)
  Placement2 = pos=(-71.4417,18.9887,0.25) rot=(-1,0,0;1.5708rad)
  Reference1 = -> Assembly [LED004.Face4,LED004.Face4]
  Reference2 = -> Assembly [LED003.Face2,LED003.Face2]
FEATURE [App::FeaturePython] Joint015  label="Fixed015"  # Assembly joint (typed FeaturePython)
  Activated = true
  AngleMax = 0
  AngleMin = 0
  Detach1 = false
  Detach2 = false
  Distance = 0
  Distance2 = 0
  EnableAngleMax = false
  EnableAngleMin = false
  EnableLengthMax = false
  EnableLengthMin = false
  JointType = 0 (Fixed)
  LengthMax = 0
  LengthMin = 0
  Offset2 = pos=(0,1.1,-2.25) rot=(0,0,1;0rad)
  Placement1 = pos=(-70.8167,22.2387,0) rot=(0.57735,0.57735,0.57735;4.18879rad)
  Placement2 = pos=(-65.9111,14.8705,0) rot=(-0.57735,-0.57735,0.57735;4.18879rad)
  Reference1 = -> Assembly [LED003.Edge9,LED003.Edge9]
  Reference2 = -> Assembly [Board.Edge21,Board.Edge21]
FEATURE [App::FeaturePython] Joint016  label="Fixed016"  # Assembly joint (typed FeaturePython)
  Activated = true
  AngleMax = 0
  AngleMin = 0
  Detach1 = false
  Detach2 = false
  Distance = 0
  Distance2 = 0
  EnableAngleMax = false
  EnableAngleMin = false
  EnableLengthMax = false
  EnableLengthMin = false
  JointType = 0 (Fixed)
  LengthMax = 0
  LengthMin = 0
  Offset2 = pos=(0,0,-2) rot=(0,0,1;0rad)
  Placement1 = pos=(-71.4417,23.4887,0.25) rot=(0,-0.707107,0.707107;3.14159rad)
  Placement2 = pos=(-71.4417,18.9887,0.25) rot=(-1,0,0;1.5708rad)
  Reference1 = -> Assembly [LED001.Face4,LED001.Face4]
  Reference2 = -> Assembly [LED004.Face2,LED004.Face2]
FEATURE [App::FeaturePython] Joint017  label="Fixed017"  # Assembly joint (typed FeaturePython)
  Activated = true
  AngleMax = 0
  AngleMin = 0
  Detach1 = false
  Detach2 = false
  Distance = 0
  Distance2 = 0
  EnableAngleMax = false
  EnableAngleMin = false
  EnableLengthMax = false
  EnableLengthMin = false
  JointType = 0 (Fixed)
  LengthMax = 0
  LengthMin = 0
  Offset2 = pos=(0,0,-2) rot=(0,0,1;0rad)
  Placement1 = pos=(-71.4417,20.9887,0.25) rot=(-1,0,0;1.5708rad)
  Placement2 = pos=(-71.4417,25.4887,0.25) rot=(0,-0.707107,0.707107;3.14159rad)
  Reference1 = -> Assembly [LED.Face2,LED.Face2]
  Reference2 = -> Assembly [LED003.Face4,LED003.Face4]
FEATURE [App::FeaturePython] Joint018  label="Fixed018"  # Assembly joint (typed FeaturePython)
  Activated = true
  AngleMax = 0
  AngleMin = 0
  Detach1 = false
  Detach2 = false
  Distance = 0
  Distance2 = 0
  EnableAngleMax = false
  EnableAngleMin = false
  EnableLengthMax = false
  EnableLengthMin = false
  JointType = 0 (Fixed)
  LengthMax = 0
  LengthMin = 0
  Offset2 = pos=(0,0,-7.5) rot=(0,0,1;0rad)
  Placement1 = pos=(-71.4417,20.9887,0.25) rot=(-1,0,0;1.5708rad)
  Placement2 = pos=(-71.4417,30.9887,0.25) rot=(0,-0.707107,0.707107;3.14159rad)
  Reference1 = -> Assembly [LED002.Face2,LED002.Face2]
  Reference2 = -> Assembly [LED.Face4,LED.Face4]
FEATURE [App::FeaturePython] Joint019  label="Fixed019"  # Assembly joint (typed FeaturePython)
  Activated = true
  AngleMax = 0
  AngleMin = 0
  Detach1 = false
  Detach2 = false
  Distance = 0
  Distance2 = 0
  EnableAngleMax = false
  EnableAngleMin = false
  EnableLengthMax = false
  EnableLengthMin = false
  JointType = 0 (Fixed)
  LengthMax = 0
  LengthMin = 0
  Offset2 = pos=(0,18.5,2.2) rot=(0,0,1;0rad)
  Placement1 = pos=(-71.4417,23.4887,0.5) rot=(-0.707107,0,0.707107;3.14159rad)
  Placement2 = pos=(-48.5111,-14.5795,0) rot=(-0.57735,-0.57735,0.57735;4.18879rad)
  Reference1 = -> Assembly [LED005.Edge12,LED005.Edge12]
  Reference2 = -> Assembly [Board.Edge21,Board.Vertex15]
FEATURE [App::FeaturePython] Joint020  label="Fixed020"  # Assembly joint (typed FeaturePython)
  Activated = true
  AngleMax = 0
  AngleMin = 0
  Detach1 = false
  Detach2 = false
  Distance = 0
  Distance2 = 0
  EnableAngleMax = false
  EnableAngleMin = false
  EnableLengthMax = false
  EnableLengthMin = false
  JointType = 0 (Fixed)
  LengthMax = 0
  LengthMin = 0
  Offset2 = pos=(0,0,-2.5) rot=(0,0,1;0rad)
  Placement1 = pos=(-71.4417,23.4887,0.25) rot=(0,-0.707107,0.707107;3.14159rad)
  Placement2 = pos=(-71.4417,18.4887,0.25) rot=(-1,0,0;1.5708rad)
  Reference1 = -> Assembly [LED006.Face4,LED006.Face4]
  Reference2 = -> Assembly [LED005.Face2,LED005.Face2]
FEATURE [Assembly::JointGroup] Joints
  Group = -> [GroundedJoint,Joint,Joint001,Joint002,Joint003,Joint004,Joint005,Joint006,Joint007,Joint008,Joint009,Joint010,Joint011,Joint012,Joint013,Joint014,Joint015,Joint016,Joint017,Joint018,Joint019,Joint020]
FEATURE [Assembly::AssemblyObject] Assembly  label="UPS"
  Group = -> [Joints,Board,GroundedJoint,_8650_Battery_Holder,Screw_Insert,Screw_Insert001,Screw_Insert002,Screw_Insert003,Joint,Joint001,Joint002,Joint003,XH_2_54_2p007,XH_2_54_2p008,Joint004,Joint005,Joint006,_8650_v1,_8650_v002,Joint007,Joint008,Button,Spacer,Spacer001,Spacer002,Spacer003,Joint009,Joint010,Joint011,Joint012,Joint013,LED,LED001,LED002,LED003,LED004,LED005,LED006,Joint014,Joint015,Joint016,+4 more]
  Origin = -> Origin005
  Type = Assembly
